# Revit family: Building-IEC309Connections-GEWISS-67IB-INTERLOCKED-SOCKET-OUTLETS_IP67_WITH_BOTTOM_MOD
name_source: partatom
category: Apparecchi elettrici
units: mm (PartAtom-declared; Revit-internal decimal feet)

## family parameters
Condiviso = Sì
Host = Superficie
Mantenere orientamento annotazione = Sì
Punto di calcolo locali = Sì
Quota connettore circolare = Usa diametro
Taglio con vuoti quando caricato = Sì
Tipo di parte = Normale

## types (18) — shared parameters
Catalogue = BUILDING
Catalogue Range = 67 IB
Circuit breaker = MT 6 kA C characteristic
Corpo presa = Light Blue
Electrocod = 2222
Frequency = 50/60 Hz
Glow Wire Test = 850 °C (IB socket) - 650 °C (bottom)
Glow wire test: = 850 °C (IB socket) - 650 °C (bottom)
IDF = 46090be9-39b2-469a-9d50-dda3f0fea139
IDT = eae14658-a5a4-4161-b788-45d16122de7f
IP degree = IP67
Immagine tipo = B.jpg
Operating temperature: = -25 +40 °C
Produttore = GEWISS S.p.A.
Prospetto di default = 1219 mm
Protection = MCB
Rated frequency (Hz) = 50/60 Hz
SEO = Socket outlet
Shock resistance = IK08
Simbolo presa = PRESAINDSTAGNA : 3P
Struttura = Grigio RAL - 7035
Technical sheet = https://www.gewiss.com
Thermo-pressure with ball = 125 °C (IB socket) - 80 °C (bottom)
Typology = Vertical
URL = https://www.gewiss.com
Version file RFA = 21.4
With back-mounting box = Yes
Working temperature = -25 ÷ +40 °C
presa = Grigio RAL - 7035
zero-valued in all types: giallo

## per-type parameters (varying)
| type | Colour | Colour: | Descrizione | EAN code | Modello | No. of poles | Number of poles | Rated current (A) | Rated current (In) | Rated voltage | Rated voltage: | Reference h |
| GW66055N - 3P+E16A230V V.INT.SOCK.O.WB.9H MT60 IP67 | Blue | Blue | 3P+E16A230V V.INT.SOCK.O.WB.9H MT60 IP67 | 8011564740846 | GW66055N | 3P+E | 3P+E | 16 | 16 | 200 - 250 V | 200 - 250 V | 9 |
| GW66068N - 2P+E32A400V V.INT.SOCK.O.WB.9H MT60 IP67 | Red | Red | 2P+E32A400V V.INT.SOCK.O.WB.9H MT60 IP67 | 8011564740938 | GW66068N | 2P+E | 2P+E | 32 | 32 | 380 - 415 V | 380 - 415 V | 9 |
| GW66065N - 2P+E32A230V V.INT.SOCK.O.WB.6H MT60 IP67 | Blue | Blue | 2P+E32A230V V.INT.SOCK.O.WB.6H MT60 IP67 | 8011564742505 | GW66065N | 2P+E | 2P+E | 32 | 32 | 200 - 250 V | 200 - 250 V | 6 |
| GW66067N - 3P+N+E32A230V V.IN.SOC.O.WB.9H MT60 IP67 | Blue | Blue | 3P+N+E32A230V V.IN.SOC.O.WB.9H MT60 IP67 | 8011564740921 | GW66067N | 3P+N+E | 3P+N+E | 32 | 32 | 200 - 250 V | 200 - 250 V | 9 |
| GW66070N - 3P+N+E32A400V V.IN.SOC.O.WB.6H MT60 IP67 | Red | Red | 3P+N+E32A400V V.IN.SOC.O.WB.6H MT60 IP67 | 8011564740952 | GW66070N | 3P+N+E | 3P+N+E | 32 | 32 | 380 - 415 V | 380 - 415 V | 6 |
| GW66053N - 3P+N+E16A110V V.IN.SOC.O.WB.4H MT60 IP67 | Yellow | Yellow | 3P+N+E16A110V V.IN.SOC.O.WB.4H MT60 IP67 | 8011564740839 | GW66053N | 3P+N+E | 3P+N+E | 16 | 16 | 100 - 130 V | 100 - 130 V | 4 |
| GW66056N - 3P+N+E16A230V V.IN.SOC.O.WB.9H MT60 IP67 | Blue | Blue | 3P+N+E16A230V V.IN.SOC.O.WB.9H MT60 IP67 | 8011564740853 | GW66056N | 3P+N+E | 3P+N+E | 16 | 16 | 200 - 250 V | 200 - 250 V | 9 |
| GW66063N - 3P+E32A110V V.INT.SOCK.O.WB.4H MT60 IP67 | Yellow | Yellow | 3P+E32A110V V.INT.SOCK.O.WB.4H MT60 IP67 | 8011564740891 | GW66063N | 3P+E | 3P+E | 32 | 32 | 100 - 130 V | 100 - 130 V | 4 |
| GW66069N - 3P+E32A400V V.INT.SOCK.O.WB.6H MT60 IP67 | Red | Red | 3P+E32A400V V.INT.SOCK.O.WB.6H MT60 IP67 | 8011564740945 | GW66069N | 3P+E | 3P+E | 32 | 32 | 380 - 415 V | 380 - 415 V | 6 |
| GW66057N - 2P+E16A400V V.INT.SOCK.O.WB.9H MT60 IP67 | Red | Red | 2P+E16A400V V.INT.SOCK.O.WB.9H MT60 IP67 | 8011564740860 | GW66057N | 2P+E | 2P+E | 16 | 16 | 380 - 415 V | 380 - 415 V | 9 |
| GW66054N - 2P+E16A230V V.INT.SOCK.O.WB.6H MT60 IP67 | Blue | Blue | 2P+E16A230V V.INT.SOCK.O.WB.6H MT60 IP67 | 8011564742482 | GW66054N | 2P+E | 2P+E | 16 | 16 | 200 - 250 V | 200 - 250 V | 6 |
| GW66064N - 3P+N+E32A110V V.IN.SOC.O.WB.4H MT60 IP67 | Yellow | Yellow | 3P+N+E32A110V V.IN.SOC.O.WB.4H MT60 IP67 | 8011564740907 | GW66064N | 3P+N+E | 3P+N+E | 32 | 32 | 100 - 130 V | 100 - 130 V | 4 |
| GW66051N - 2P+E16A110V V.INT.SOCK.O.WB.4H MT60 IP67 | Yellow | Yellow | 2P+E16A110V V.INT.SOCK.O.WB.4H MT60 IP67 | 8011564740815 | GW66051N | 2P+E | 2P+E | 16 | 16 | 100 - 130 V | 100 - 130 V | 4 |
| GW66066N - 3P+E32A230V V.INT.SOCK.O.WB.9H MT60 IP67 | Blue | Blue | 3P+E32A230V V.INT.SOCK.O.WB.9H MT60 IP67 | 8011564740914 | GW66066N | 3P+E | 3P+E | 32 | 32 | 200 - 250 V | 200 - 250 V | 9 |
| GW66058N - 3P+E16A400V V.INT.SOCK.O.WB.6H MT60 IP67 | Red | Red | 3P+E16A400V V.INT.SOCK.O.WB.6H MT60 IP67 | 8011564740877 | GW66058N | 3P+E | 3P+E | 16 | 16 | 380 - 415 V | 380 - 415 V | 6 |
| GW66059N - 3P+N+E16A400V V.IN.SOC.O.WB.6H MT60 IP67 | Red | Red | 3P+N+E16A400V V.IN.SOC.O.WB.6H MT60 IP67 | 8011564742499 | GW66059N | 3P+N+E | 3P+N+E | 16 | 16 | 380 - 415 V | 380 - 415 V | 6 |
| GW66052N - 3P+E16A110V V.INT.SOCK.O.WB.4H MT60 IP67 | Yellow | Yellow | 3P+E16A110V V.INT.SOCK.O.WB.4H MT60 IP67 | 8011564740822 | GW66052N | 3P+E | 3P+E | 16 | 16 | 100 - 130 V | 100 - 130 V | 4 |
| GW66062N - 2P+E32A110V V.INT.SOCK.O.WB.4H MT60 IP67 | Yellow | Yellow | 2P+E32A110V V.INT.SOCK.O.WB.4H MT60 IP67 | 8011564740884 | GW66062N | 2P+E | 2P+E | 32 | 32 | 100 - 130 V | 100 - 130 V | 4 |

## geometry (parser evidence)
native form markers: Sweep x3
no freeform markers — native parametric forms only
